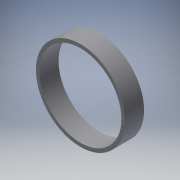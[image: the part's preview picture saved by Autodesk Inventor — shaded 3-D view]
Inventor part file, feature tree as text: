
AUTODESK INVENTOR PART (.ipt)
format: ipt  version: 2017 (Build 210142000, 142)  size: 104,448 bytes
history: native  units: in
note: dims shown in document units (in); Inventor stores cm internally (conversion verified against a paired STEP export)
features: other x3, reference x2, sketch x1, plane x1, extrude x1
ambient origin geometry x8: Origin, YZ Plane, XZ Plane, XY Plane, X Axis, Y Axis, Z Axis, Center Point
bodies: Solid1 (feature_tree)
feature tree (8):
  sketch  "Sketch1"  dims[d1=1.0in d2=0.0in d3=0.02in]
  plane  "Work Plane1"
  extrude  "Extrusion1"  Depth=0.02in
  reference  "Reference1"
  reference  "Reference2"
  other  "<userpath>\Documents\Inventor\PixyCam and Gimbal\PIXYWITHRING.iam"
  other  "PIXYWITHRING.iam"
  other  "PixyCamKinda:1"
